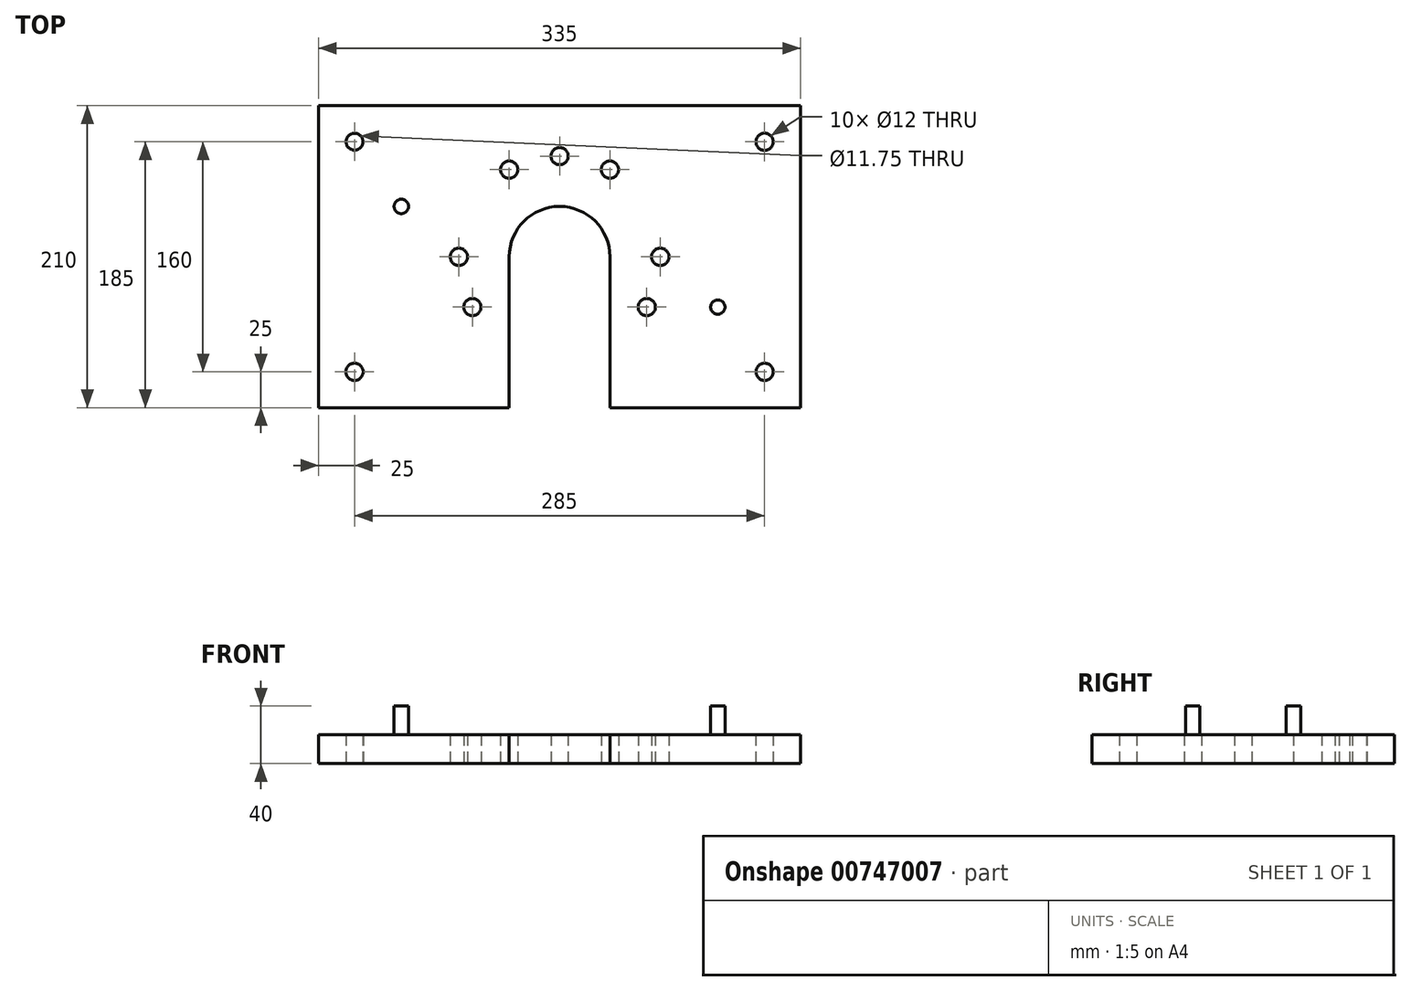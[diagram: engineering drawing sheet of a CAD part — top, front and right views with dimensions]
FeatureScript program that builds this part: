
annotation { "Feature Type Name" : "Feature", "Feature Type Description" : "" }
export const myFeature = defineFeature(function(context is Context, id is Id, definition is map)
    precondition{}
    {
        {
            var Q0;
            Q0=qCreatedBy(makeId("Top.planeOp"),FACE);
            var sketch = newSketch(context, id + "F0", { "sketchPlane" : qUnion([Q0])});
            skLineSegment(sketch, "E0.bottom", {"start": v(-167.5, 105) * mm, "end": v(167.5, 105) * mm});
            skLineSegment(sketch, "E0.top", {"start": v(-167.5, -105) * mm, "end": v(-35, -105) * mm});
            skLineSegment(sketch, "E0.left", {"start": v(-167.5, 105) * mm, "end": v(-167.5, -105) * mm});
            skLineSegment(sketch, "E0.right", {"start": v(167.5, 105) * mm, "end": v(167.5, -105) * mm});
            skArc(sketch, "E1", {"start": v(35, 0) * mm, "mid": v(0, 35) * mm, "end": v(-35, 0) * mm});
            skCircle(sketch, "E2", {"center": v(0, 0) * mm, "radius": 70 * mm, "construction": true});
            skLineSegment(sketch, "E3.left", {"start": v(-35, 0) * mm, "end": v(-35, -105) * mm});
            skLineSegment(sketch, "E3.right", {"start": v(35, 0) * mm, "end": v(35, -105) * mm});
            skLineSegment(sketch, "E4.trimOffspring", {"start": v(35, -105) * mm, "end": v(167.5, -105) * mm});
            skLineSegment(sketch, "E5.bottom", {"start": v(140, 13.45) * mm, "end": v(152.7, 13.45) * mm, "construction": true});
            skLineSegment(sketch, "E5.top", {"start": v(140, -13.45) * mm, "end": v(152.7, -13.45) * mm, "construction": true});
            skLineSegment(sketch, "E5.left", {"start": v(140, 13.45) * mm, "end": v(140, -13.45) * mm, "construction": true});
            skLineSegment(sketch, "E5.right", {"start": v(152.7, 13.45) * mm, "end": v(152.7, -13.45) * mm, "construction": true});
            skLineSegment(sketch, "E6.bottom", {"start": v(-152.7, 13.45) * mm, "end": v(-140, 13.45) * mm, "construction": true});
            skLineSegment(sketch, "E6.top", {"start": v(-152.7, -13.45) * mm, "end": v(-140, -13.45) * mm, "construction": true});
            skLineSegment(sketch, "E6.left", {"start": v(-152.7, 13.45) * mm, "end": v(-152.7, -13.45) * mm, "construction": true});
            skLineSegment(sketch, "E6.right", {"start": v(-140, 13.45) * mm, "end": v(-140, -13.45) * mm, "construction": true});
            skCircle(sketch, "E7", {"center": v(-110, 35) * mm, "radius": 5 * mm});
            skCircle(sketch, "E8", {"center": v(110, -35) * mm, "radius": 5 * mm});
            skCircle(sketch, "E9", {"center": v(142.5, -80) * mm, "radius": 6 * mm});
            skCircle(sketch, "E10", {"center": v(142.5, 80) * mm, "radius": 6 * mm});
            skCircle(sketch, "E11", {"center": v(-142.5, -80) * mm, "radius": 6 * mm});
            skCircle(sketch, "E12", {"center": v(-142.5, 80) * mm, "radius": 5.87 * mm});
            skCircle(sketch, "E13", {"center": v(-70, 0) * mm, "radius": 6 * mm});
            skCircle(sketch, "E14.1.0", {"center": v(-60.62, -35) * mm, "radius": 6 * mm});
            skCircle(sketch, "E14.5.0", {"center": v(60.62, -35) * mm, "radius": 6 * mm});
            skCircle(sketch, "E14.6.0", {"center": v(70, 0) * mm, "radius": 6 * mm});
            skCircle(sketch, "E14.8.0", {"center": v(35, 60.62) * mm, "radius": 6 * mm});
            skCircle(sketch, "E14.9.0", {"center": v(0, 70) * mm, "radius": 6 * mm});
            skCircle(sketch, "E14.10.0", {"center": v(-35, 60.62) * mm, "radius": 6 * mm});
            skSolve(sketch);
        }
        {
            var Q0;
            Q0=makeQuery(id+"F0.imprint","IMPRINT",FACE,{"disambiguationData":[TD([[makeQuery(id+"F0.imprint","IMPRINT",EDGE,{"derivedFrom":sQuery(id+"F0.wireOp",EDGE,"E0.bottom")}),-1.0]])]});
            extrude(context, id + "F1", {"entities" : qUnion([Q0]), "depth" : 20 * mm, "offsetDistance" : 25 * mm});
        }
        {
            var Q0;
            Q0=makeQuery(id+"F0.imprint","IMPRINT",FACE,{"disambiguationData":[TD([[makeQuery(id+"F0.imprint","IMPRINT",EDGE,{"derivedFrom":sQuery(id+"F0.wireOp",EDGE,"E7")}),1.0]])]});
            var Q1;
            Q1=makeQuery(id+"F0.imprint","IMPRINT",FACE,{"disambiguationData":[TD([[makeQuery(id+"F0.imprint","IMPRINT",EDGE,{"derivedFrom":sQuery(id+"F0.wireOp",EDGE,"E8")}),1.0]])]});
            extrude(context, id + "F2", {"entities" : qUnion([Q0, Q1]), "operationType" : NewBodyOperationType.ADD, "depth" : 40 * mm, "offsetDistance" : 25 * mm});
        }
    });
